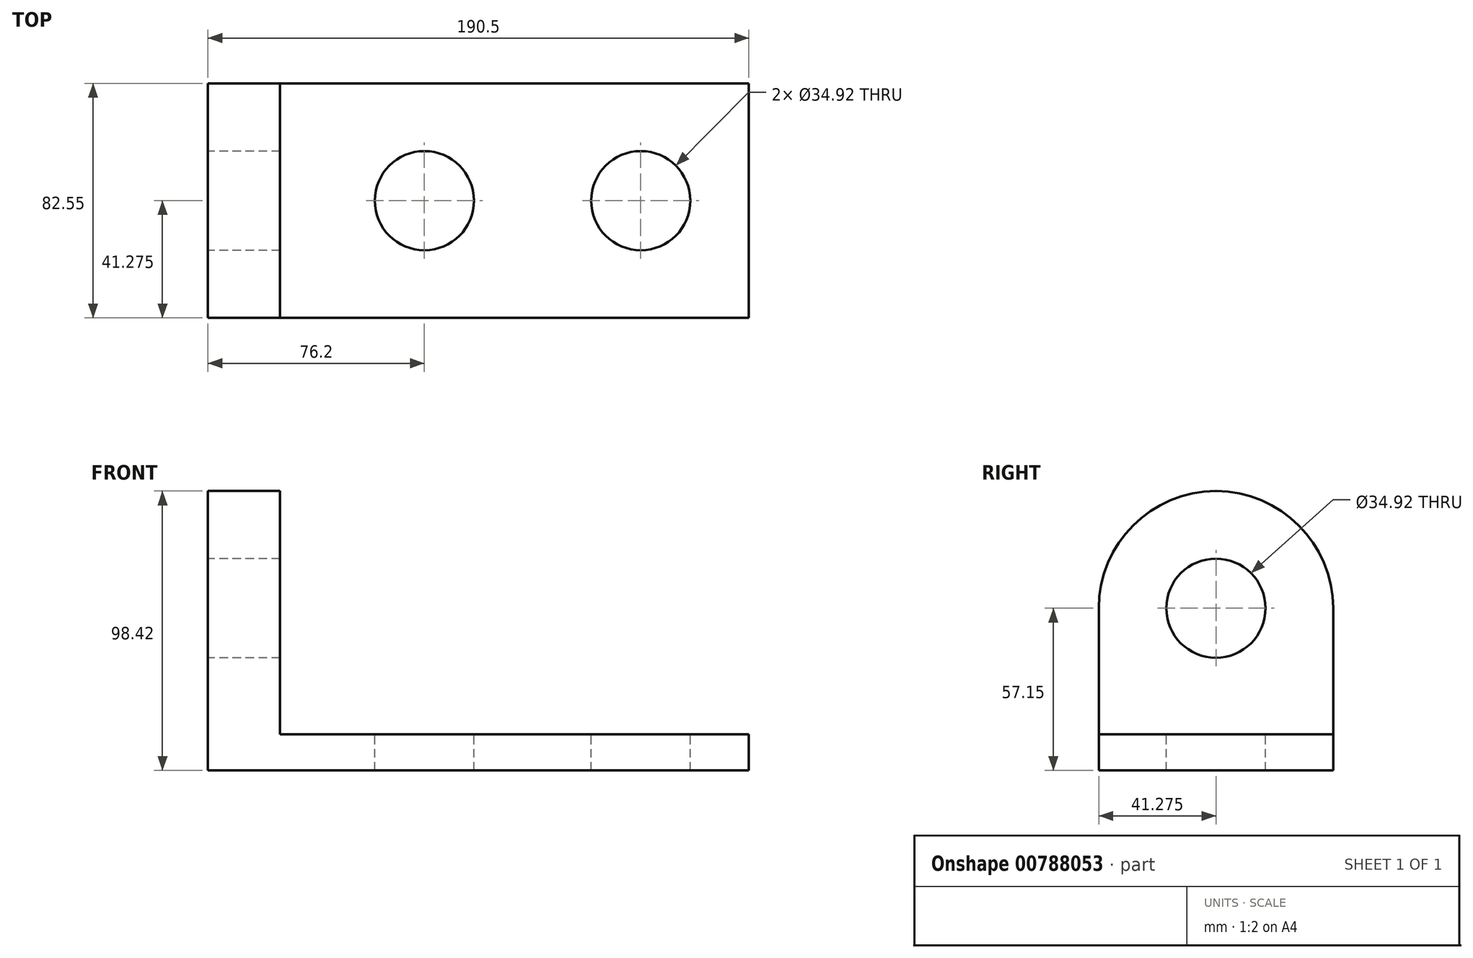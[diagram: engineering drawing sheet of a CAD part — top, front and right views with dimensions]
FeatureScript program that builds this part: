
annotation { "Feature Type Name" : "Feature", "Feature Type Description" : "" }
export const myFeature = defineFeature(function(context is Context, id is Id, definition is map)
    precondition{}
    {
        {
            var Q0;
            Q0=qCreatedBy(makeId("Right.planeOp"),FACE);
            var sketch = newSketch(context, id + "F0", { "sketchPlane" : qUnion([Q0])});
            skLineSegment(sketch, "E0", {"start": v(0, 0) * mm, "end": v(82.55, 0) * mm});
            skLineSegment(sketch, "E1", {"start": v(82.55, 0) * mm, "end": v(82.55, 57.15) * mm});
            skLineSegment(sketch, "E2", {"start": v(82.55, 57.15) * mm, "end": v(0, 57.15) * mm});
            skLineSegment(sketch, "E3", {"start": v(0, 57.15) * mm, "end": v(0, 0) * mm});
            skLineSegment(sketch, "E4", {"start": v(0, 0) * mm, "end": v(0, 12.7) * mm});
            skLineSegment(sketch, "E5", {"start": v(0, 12.7) * mm, "end": v(82.55, 12.7) * mm});
            skArc(sketch, "E6", {"start": v(82.55, 57.15) * mm, "mid": v(41.28, 98.43) * mm, "end": v(0, 57.15) * mm});
            skCircle(sketch, "E7", {"center": v(41.28, 57.15) * mm, "radius": 17.46 * mm});
            skSolve(sketch);
        }
        {
            var Q0;
            {var subQ0=sQuery(id+"F0.wireOp",EDGE,"E0");Q0=makeQuery(id+"F0.imprint","IMPRINT",FACE,{"disambiguationData":[TD([[makeQuery(id+"F0.imprint","IMPRINT",EDGE,{"derivedFrom":subQ0}),1.0]])]});}
            extrude(context, id + "F1", {"entities" : qUnion([Q0]), "depth" : 190.5 * mm, "offsetDistance" : 25.4 * mm});
        }
        {
            var Q0;
            {var subQ9=sQuery(id+"F0.wireOp",EDGE,"E5");Q0=makeQuery(id+"F0.imprint","IMPRINT",FACE,{"disambiguationData":[TD([[makeQuery(id+"F0.imprint","IMPRINT",EDGE,{"derivedFrom":subQ9}),1.0]])]});}
            var Q1;
            {var subQ3=sQuery(id+"F0.wireOp",EDGE,"E6");Q1=makeQuery(id+"F0.imprint","IMPRINT",FACE,{"disambiguationData":[TD([[makeQuery(id+"F0.imprint","IMPRINT",EDGE,{"derivedFrom":subQ3}),1.0]])]});}
            extrude(context, id + "F2", {"entities" : qUnion([Q0, Q1]), "operationType" : NewBodyOperationType.ADD, "depth" : 25.4 * mm, "offsetDistance" : 25.4 * mm});
        }
        {
            var Q0;
            Q0=makeQuery(id+"F1.opExtrude","SWEPT_FACE",FACE,{"disambiguationData":[OSD([sQuery(id+"F0.wireOp",EDGE,"E5")])]});
            var sketch = newSketch(context, id + "F3", { "sketchPlane" : qUnion([Q0])});
            skLineSegment(sketch, "E8", {"start": v(190.5, 41.28) * mm, "end": v(152.4, 41.28) * mm, "construction": true});
            skLineSegment(sketch, "E9", {"start": v(152.4, 41.28) * mm, "end": v(76.2, 41.28) * mm, "construction": true});
            skCircle(sketch, "E10", {"center": v(76.2, 41.28) * mm, "radius": 17.46 * mm});
            skCircle(sketch, "E11", {"center": v(152.4, 41.28) * mm, "radius": 17.46 * mm});
            skSolve(sketch);
        }
        {
            var Q0;
            Q0=makeQuery(id+"F3.imprint","IMPRINT",FACE,{"disambiguationData":[TD([[makeQuery(id+"F3.imprint","IMPRINT",EDGE,{"derivedFrom":sQuery(id+"F3.wireOp",EDGE,"E10")}),1.0]])]});
            var Q1;
            Q1=makeQuery(id+"F3.imprint","IMPRINT",FACE,{"disambiguationData":[TD([[makeQuery(id+"F3.imprint","IMPRINT",EDGE,{"derivedFrom":sQuery(id+"F3.wireOp",EDGE,"E11")}),1.0]])]});
            extrude(context, id + "F4", {"entities" : qUnion([Q0, Q1]), "operationType" : NewBodyOperationType.REMOVE, "endBound" : BoundingType.UP_TO_NEXT, "oppositeDirection" : true, "depth" : -mm, "offsetDistance" : 25.4 * mm});
        }
    });
